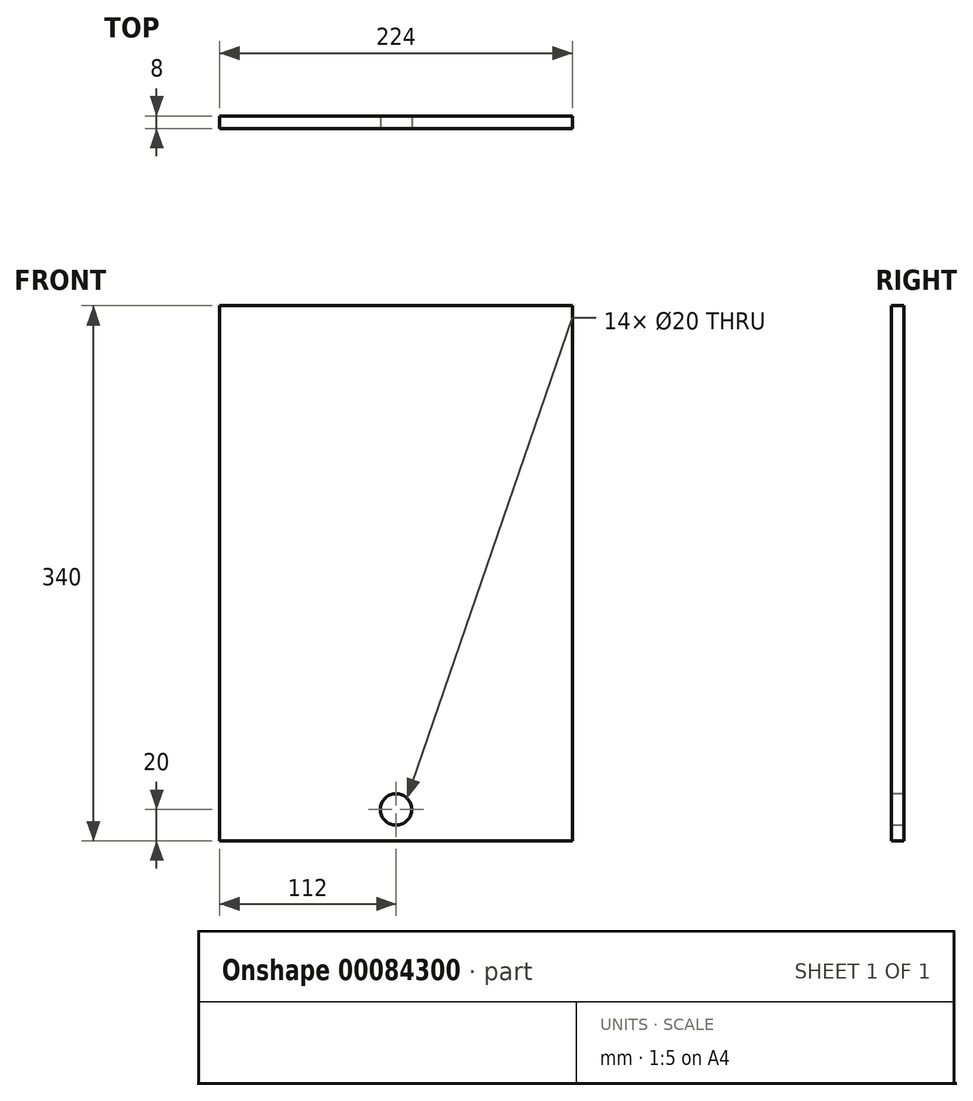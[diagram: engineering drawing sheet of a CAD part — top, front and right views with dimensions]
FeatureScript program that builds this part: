
annotation { "Feature Type Name" : "Feature", "Feature Type Description" : "" }
export const myFeature = defineFeature(function(context is Context, id is Id, definition is map)
    precondition{}
    {
        {
            var Q0;
            Q0=qCreatedBy(makeId("Front.planeOp"),FACE);
            var sketch = newSketch(context, id + "F0", { "sketchPlane" : qUnion([Q0])});
            skLineSegment(sketch, "E0.bottom", {"start": v(-112, 170) * mm, "end": v(112, 170) * mm});
            skLineSegment(sketch, "E0.top", {"start": v(-112, -170) * mm, "end": v(112, -170) * mm});
            skLineSegment(sketch, "E0.left", {"start": v(-112, 170) * mm, "end": v(-112, -170) * mm});
            skLineSegment(sketch, "E0.right", {"start": v(112, 170) * mm, "end": v(112, -170) * mm});
            skPoint(sketch, "E0.middle", {"position": v(0, 0) * mm});
            skSolve(sketch);
        }
        {
            var Q0;
            Q0=makeQuery(id+"F0.imprint","IMPRINT",FACE,{"disambiguationData":[TD([[makeQuery(id+"F0.imprint","IMPRINT",EDGE,{"derivedFrom":sQuery(id+"F0.wireOp",EDGE,"E0.bottom")}),-1.0]])]});
            var Q1;
            Q1 = qSketchRegion(id + "F2", true);
            extrude(context, id + "F1", {"entities" : qUnion([Q0, Q1]), "depth" : 8 * mm, "offsetDistance" : 25 * mm});
        }
        {
            var Q0;
            Q0=makeQuery(id+"F1.opExtrude","CAP_FACE",FACE,{"disambiguationData":[OSD([sQuery(id+"F0.wireOp",EDGE,"E0.bottom"),sQuery(id+"F0.wireOp",EDGE,"E0.top"),sQuery(id+"F0.wireOp",EDGE,"E0.left"),sQuery(id+"F0.wireOp",EDGE,"E0.right")])],"isStart":false});
            var sketch = newSketch(context, id + "F2", { "sketchPlane" : qUnion([Q0])});
            skCircle(sketch, "E1", {"center": v(0, -150) * mm, "radius": 10 * mm});
            skSolve(sketch);
        }
        {
            var Q0;
            Q0=makeQuery(id+"F2.imprint","IMPRINT",FACE,{"disambiguationData":[TD([[makeQuery(id+"F2.imprint","IMPRINT",EDGE,{"derivedFrom":sQuery(id+"F2.wireOp",EDGE,"E1")}),1.0]])]});
            extrude(context, id + "F3", {"entities" : qUnion([Q0]), "operationType" : NewBodyOperationType.REMOVE, "endBound" : BoundingType.UP_TO_NEXT, "oppositeDirection" : true, "depth" : 25 * mm});
        }
    });
